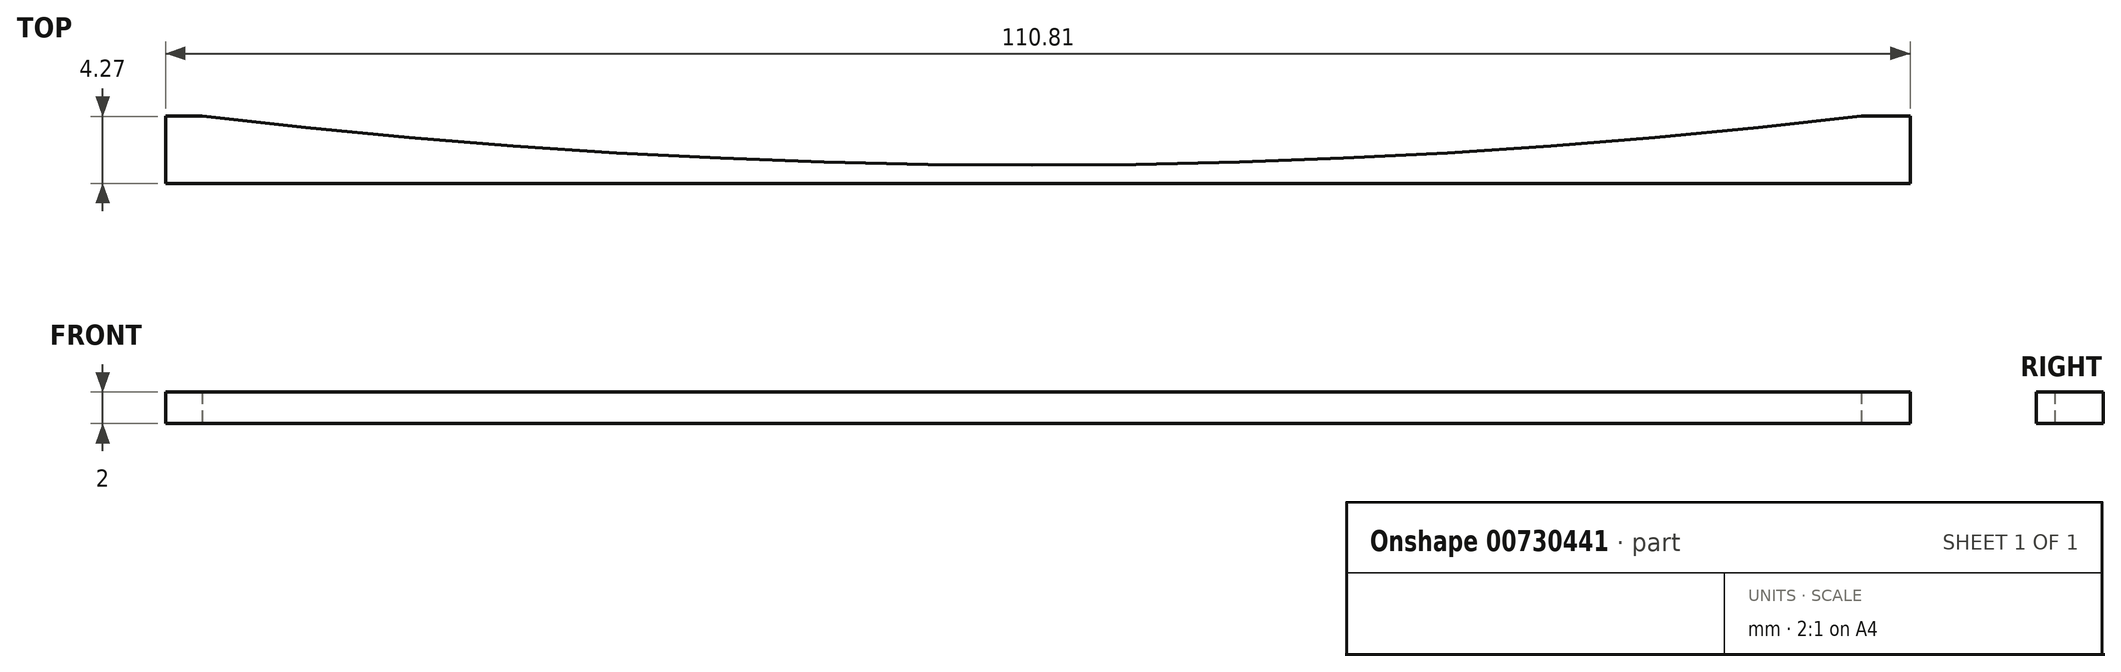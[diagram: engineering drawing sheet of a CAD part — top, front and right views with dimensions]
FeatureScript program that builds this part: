
annotation { "Feature Type Name" : "Feature", "Feature Type Description" : "" }
export const myFeature = defineFeature(function(context is Context, id is Id, definition is map)
    precondition{}
    {
        {
            var Q0;
            Q0=qCreatedBy(makeId("Top.planeOp"),FACE);
            var sketch = newSketch(context, id + "F0", { "sketchPlane" : qUnion([Q0])});
            skLineSegment(sketch, "E0.top", {"start": v(-58.57, 14.82) * mm, "end": v(52.24, 14.82) * mm});
            skLineSegment(sketch, "E0.left", {"start": v(-58.57, 19.1) * mm, "end": v(-58.57, 14.82) * mm});
            skLineSegment(sketch, "E0.right", {"start": v(52.24, 19.1) * mm, "end": v(52.24, 14.82) * mm});
            skLineSegment(sketch, "E1", {"start": v(-58.57, 19.1) * mm, "end": v(-56.23, 19.1) * mm});
            skLineSegment(sketch, "E2", {"start": v(52.24, 19.1) * mm, "end": v(49.15, 19.1) * mm});
            skArc(sketch, "E3", {"start": v(-56.23, 19.1) * mm, "mid": v(-3.54, 15.99) * mm, "end": v(49.15, 19.1) * mm});
            skSolve(sketch);
        }
        {
            var Q0;
            Q0=makeQuery(id+"F0.imprint","IMPRINT",FACE,{"disambiguationData":[TD([[makeQuery(id+"F0.imprint","IMPRINT",EDGE,{"derivedFrom":sQuery(id+"F0.wireOp",EDGE,"E0.top")}),1.0]])]});
            extrude(context, id + "F1", {"entities" : qUnion([Q0]), "depth" : 2 * mm, "offsetDistance" : 25 * mm});
        }
    });
